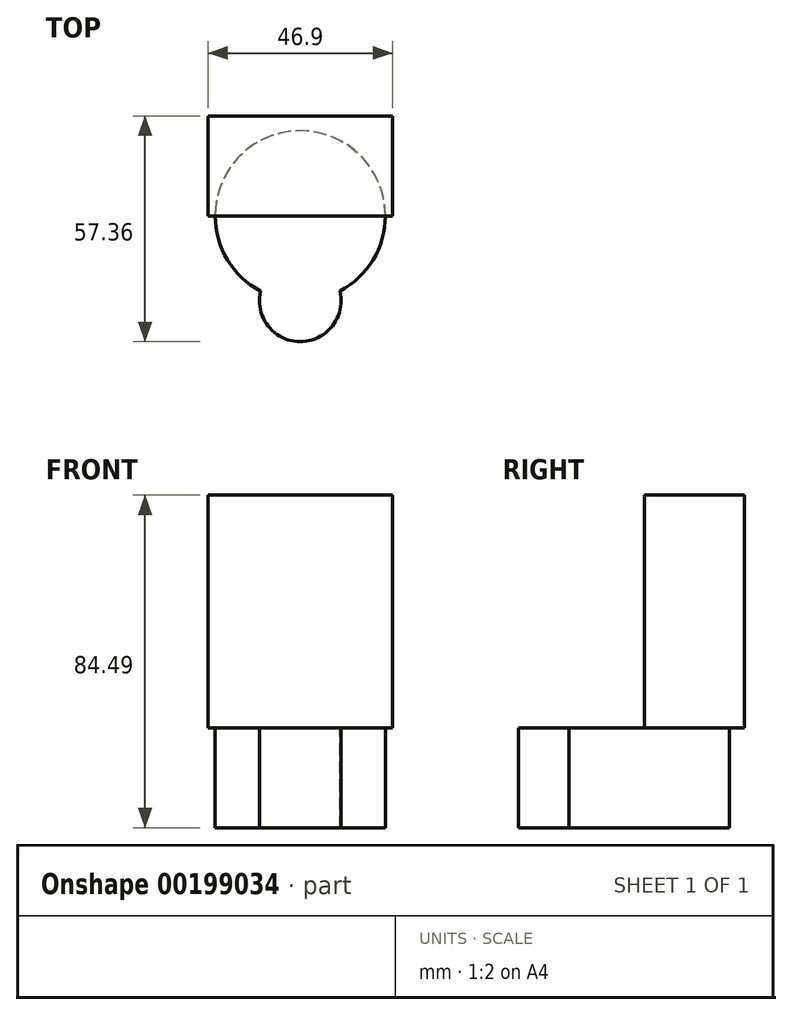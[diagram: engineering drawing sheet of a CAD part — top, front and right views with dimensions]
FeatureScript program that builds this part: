
annotation { "Feature Type Name" : "Feature", "Feature Type Description" : "" }
export const myFeature = defineFeature(function(context is Context, id is Id, definition is map)
    precondition{}
    {
        {
            var Q0;
            Q0=qCreatedBy(makeId("Front.planeOp"),FACE);
            var sketch = newSketch(context, id + "F0", { "sketchPlane" : qUnion([Q0])});
            skLineSegment(sketch, "E0.bottom", {"start": v(46.9, 59.09) * mm, "end": v(0, 59.09) * mm});
            skLineSegment(sketch, "E0.top", {"start": v(46.9, 0) * mm, "end": v(0, 0) * mm});
            skLineSegment(sketch, "E0.left", {"start": v(46.9, 59.09) * mm, "end": v(46.9, 0) * mm});
            skLineSegment(sketch, "E0.right", {"start": v(0, 59.09) * mm, "end": v(0, 0) * mm});
            skSolve(sketch);
        }
        {
            var Q0;
            Q0 = qSketchRegion(id + "F0", true);
            extrude(context, id + "F1", {"entities" : qUnion([Q0]), "depth" : 25.4 * mm});
        }
        {
            var Q0;
            Q0=makeQuery(id+"F1.opExtrude","SWEPT_FACE",FACE,{"disambiguationData":[OSD([sQuery(id+"F0.wireOp",EDGE,"E0.top")])]});
            var sketch = newSketch(context, id + "F2", { "sketchPlane" : qUnion([Q0])});
            skCircle(sketch, "E1", {"center": v(23.45, 25.4) * mm, "radius": 21.62 * mm});
            skCircle(sketch, "E2", {"center": v(23.45, 47.02) * mm, "radius": 10.34 * mm});
            skSolve(sketch);
        }
        {
            var Q0;
            Q0 = qSketchRegion(id + "F2", true);
            extrude(context, id + "F3", {"entities" : qUnion([Q0]), "operationType" : NewBodyOperationType.ADD, "depth" : 25.4 * mm});
        }
    });
